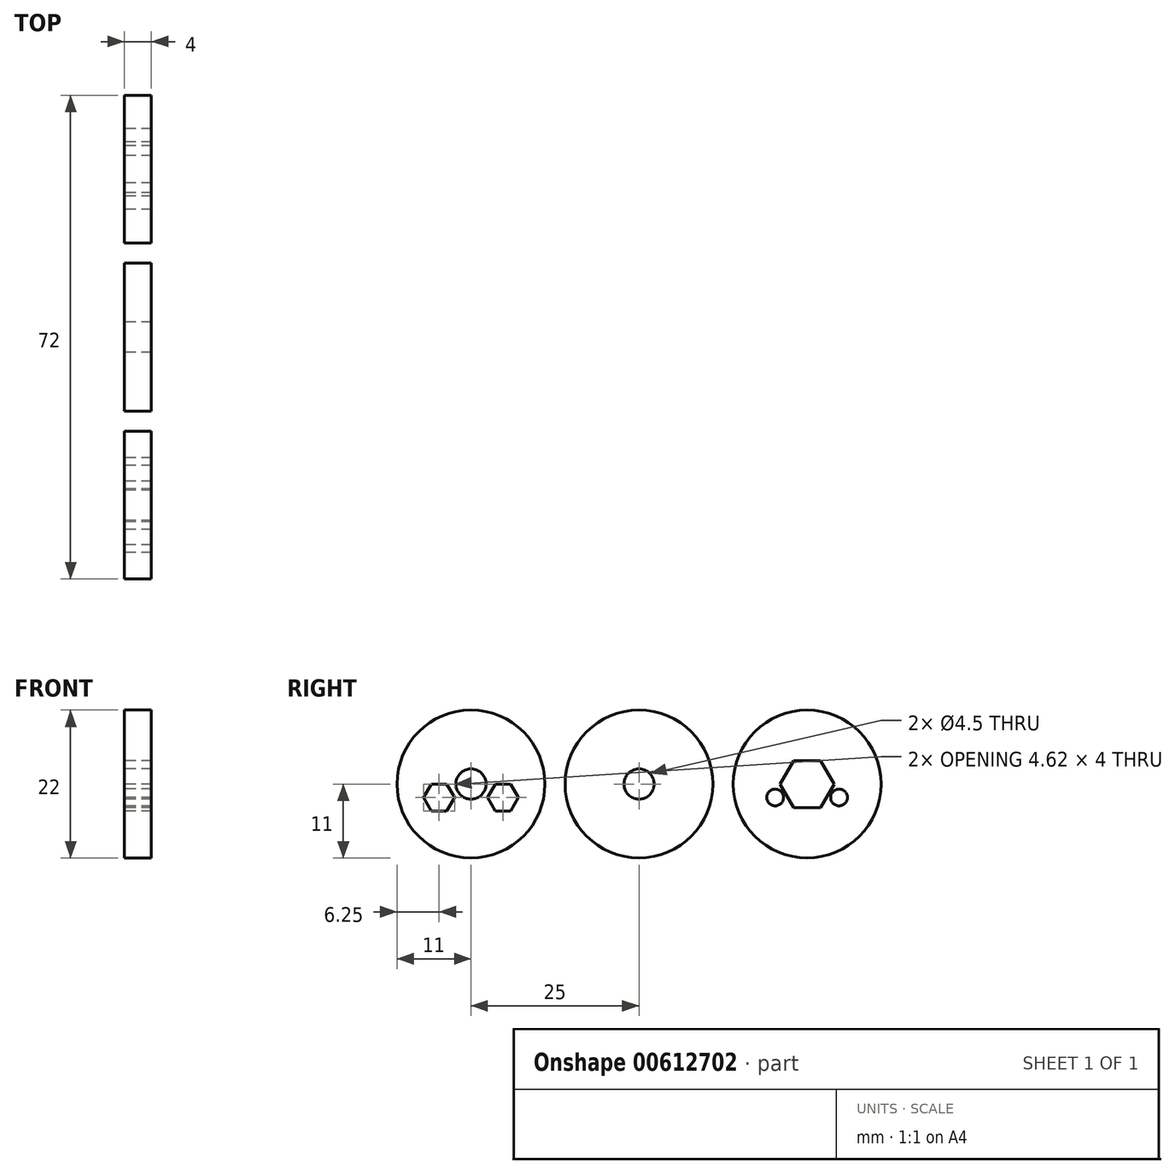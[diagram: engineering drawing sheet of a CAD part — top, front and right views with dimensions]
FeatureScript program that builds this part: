
annotation { "Feature Type Name" : "Feature", "Feature Type Description" : "" }
export const myFeature = defineFeature(function(context is Context, id is Id, definition is map)
    precondition{}
    {
        {
            var Q0;
            Q0=qCreatedBy(makeId("Right.planeOp"), FACE);
            var sketch = newSketch(context, id + "F0", { "sketchPlane" : qUnion([Q0])});
            skCircle(sketch, "E0", {"center": v(0, 0) * mm, "radius": 11 * mm});
            skCircle(sketch, "E1", {"center": v(0, 0) * mm, "radius": 2.25 * mm});
            skCircle(sketch, "E2", {"center": v(-25, 0) * mm, "radius": 2.25 * mm});
            skCircle(sketch, "E3", {"center": v(20.25, -2) * mm, "radius": 1.25 * mm});
            skCircle(sketch, "E4", {"center": v(29.75, -2) * mm, "radius": 1.25 * mm});
            skLineSegment(sketch, "E5", {"start": v(-29.75, -2) * mm, "end": v(-20.25, -2) * mm, "construction": true});
            skLineSegment(sketch, "E6", {"start": v(-25, 0) * mm, "end": v(-25, -2) * mm, "construction": true});
            skCircle(sketch, "E7.cCircle", {"center": v(-29.75, -2) * mm, "radius": 2 * mm, "construction": true});
            skLineSegment(sketch, "E7.seed", {"start": v(-28.6, 0) * mm, "end": v(-30.9, 0) * mm});
            skLineSegment(sketch, "E7.pattern.0.1.0", {"start": v(-30.9, 0) * mm, "end": v(-32.06, -2) * mm});
            skLineSegment(sketch, "E7.pattern.0.2.0", {"start": v(-32.06, -2) * mm, "end": v(-30.9, -4) * mm});
            skLineSegment(sketch, "E7.pattern.0.3.0", {"start": v(-30.9, -4) * mm, "end": v(-28.6, -4) * mm});
            skLineSegment(sketch, "E7.pattern.0.4.0", {"start": v(-28.6, -4) * mm, "end": v(-27.44, -2) * mm});
            skLineSegment(sketch, "E7.pattern.0.5.0", {"start": v(-27.44, -2) * mm, "end": v(-28.6, 0) * mm});
            skPoint(sketch, "E7.pattern.center", {"position": v(-29.75, -2) * mm});
            skPoint(sketch, "E7.midPoint", {"position": v(-29.75, 0) * mm});
            skCircle(sketch, "E8.cCircle", {"center": v(-20.25, -2) * mm, "radius": 2 * mm, "construction": true});
            skLineSegment(sketch, "E8.seed", {"start": v(-19.1, 0) * mm, "end": v(-21.4, 0) * mm});
            skLineSegment(sketch, "E8.pattern.0.1.0", {"start": v(-21.4, 0) * mm, "end": v(-22.56, -2) * mm});
            skLineSegment(sketch, "E8.pattern.0.2.0", {"start": v(-22.56, -2) * mm, "end": v(-21.4, -4) * mm});
            skLineSegment(sketch, "E8.pattern.0.3.0", {"start": v(-21.4, -4) * mm, "end": v(-19.1, -4) * mm});
            skLineSegment(sketch, "E8.pattern.0.4.0", {"start": v(-19.1, -4) * mm, "end": v(-17.94, -2) * mm});
            skLineSegment(sketch, "E8.pattern.0.5.0", {"start": v(-17.94, -2) * mm, "end": v(-19.1, 0) * mm});
            skPoint(sketch, "E8.pattern.center", {"position": v(-20.25, -2) * mm});
            skPoint(sketch, "E8.midPoint", {"position": v(-20.25, 0) * mm});
            skLineSegment(sketch, "E9", {"start": v(20.25, -2) * mm, "end": v(29.75, -2) * mm, "construction": true});
            skCircle(sketch, "E10.cCircle", {"center": v(25, 0) * mm, "radius": 3.5 * mm, "construction": true});
            skLineSegment(sketch, "E10.seed", {"start": v(27.02, 3.5) * mm, "end": v(22.98, 3.5) * mm});
            skLineSegment(sketch, "E10.pattern.0.1.0", {"start": v(22.98, 3.5) * mm, "end": v(20.96, 0) * mm});
            skLineSegment(sketch, "E10.pattern.0.2.0", {"start": v(20.96, 0) * mm, "end": v(22.98, -3.5) * mm});
            skLineSegment(sketch, "E10.pattern.0.3.0", {"start": v(22.98, -3.5) * mm, "end": v(27.02, -3.5) * mm});
            skLineSegment(sketch, "E10.pattern.0.4.0", {"start": v(27.02, -3.5) * mm, "end": v(29.04, 0) * mm});
            skLineSegment(sketch, "E10.pattern.0.5.0", {"start": v(29.04, 0) * mm, "end": v(27.02, 3.5) * mm});
            skPoint(sketch, "E10.pattern.center", {"position": v(25, 0) * mm});
            skPoint(sketch, "E10.midPoint", {"position": v(25, 3.5) * mm});
            skLineSegment(sketch, "E11", {"start": v(25, 0) * mm, "end": v(25, -2) * mm, "construction": true});
            skCircle(sketch, "E12", {"center": v(-25, 0) * mm, "radius": 11 * mm});
            skCircle(sketch, "E13", {"center": v(25, 0) * mm, "radius": 11 * mm});
            skSolve(sketch);
        }
        {
            var Q0;
            Q0 = qSketchRegion(id + "F0", true);
            extrude(context, id + "F1", {"entities" : qUnion([Q0]), "depth" : 4 * mm, "offsetDistance" : 25 * mm});
        }
    });
